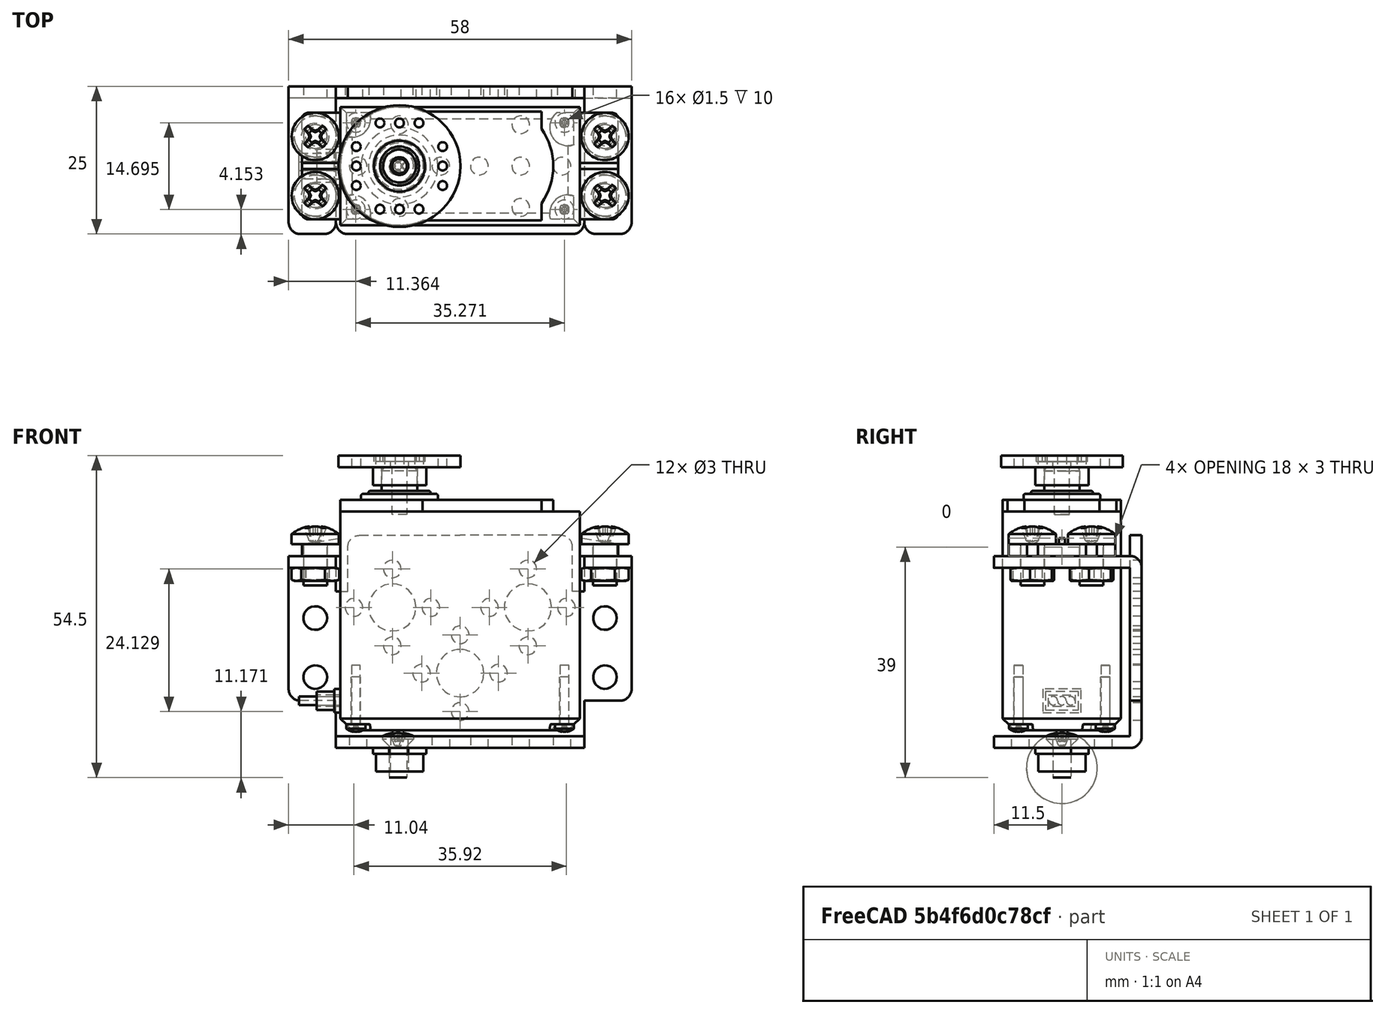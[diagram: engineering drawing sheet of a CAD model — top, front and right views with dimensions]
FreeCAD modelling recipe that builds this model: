
FCSTD DOCUMENT  (FreeCAD 0.19R24276 (Git))
Label: servo_acoplado
License: All rights reserved
LicenseURL: http://en.wikipedia.org/wiki/All_rights_reserved
objects: Part::FeaturePython×13, App::FeaturePython×12, App::DocumentObjectGroup×2
note: 13 computed .brp shape members not serialized (recipe doc carries the construction recipe); baked Part::Feature solids carry a one-line shape summary decoded from their .brp

FEATURE [Part::FeaturePython] b_servo_001_  label="servo_001"  # a2plus imported part (geometry in sourceFile) (typed FeaturePython)
  a2p_Version = V0.1
  fixedPosition = true
  objectType = a2pPart
  sourceFile = .\..\piezas\servo.FCStd
  subassemblyImport = false
  timeLastImport = 1.6204e+09
  updateColors = true
FEATURE [Part::FeaturePython] b_parte_servos_001_  label="parte_servos_001"  # a2plus imported part (geometry in sourceFile) (typed FeaturePython)
  Placement = pos=(2.597e-07,13.5,15) rot=(1,0,0;1.5708rad)
  a2p_Version = V0.1
  fixedPosition = false
  objectType = a2pPart
  sourceFile = .\..\piezas\parte_servos.FCStd
  subassemblyImport = false
  timeLastImport = 1.62041e+09
  updateColors = true
FEATURE [Part::FeaturePython] b_arandela_001_  label="arandela_001"  # a2plus imported part (geometry in sourceFile) (typed FeaturePython)
  Placement = pos=(-10.25,3.87576e-07,-3) rot=(0,1,0;3.14159rad)
  a2p_Version = V0.1
  fixedPosition = false
  objectType = a2pPart
  sourceFile = .\..\piezas\arandela.FCStd
  subassemblyImport = false
  timeLastImport = 1.62024e+09
  updateColors = true
FEATURE [Part::FeaturePython] b_tapa_001_  label="tapa_001"  # a2plus imported part (geometry in sourceFile) (typed FeaturePython)
  Placement = pos=(-10.25,-6.82e-14,46.5) rot=(1,0,0;3.14159rad)
  a2p_Version = V0.1
  fixedPosition = false
  objectType = a2pPart
  sourceFile = .\..\piezas\tapa.FCStd
  subassemblyImport = false
  timeLastImport = 1.62021e+09
  updateColors = true
FEATURE [App::FeaturePython] planeCoincident_001  label="planeCoincident_001__parte_servos_001"  # a2plus constraint (typed FeaturePython)
  Object1 = b_servo_001_
  Object2 = b_parte_servos_001_
  ParentTreeObject = -> b_servo_001_
  SubElement1 = Face61
  SubElement2 = Face84
  Suppressed = false
  Type = plane
  directionConstraint = 1
  offset = 0
FEATURE [App::FeaturePython] planeCoincident_001_mirror  label="planeCoincident_001__servo_001"  # a2plus constraint (typed FeaturePython)
  Object1 = b_servo_001_
  Object2 = b_parte_servos_001_
  ParentTreeObject = -> b_parte_servos_001_
  SubElement1 = Face61
  SubElement2 = Face84
  Suppressed = false
  Type = plane
  directionConstraint = 1
  offset = 0
FEATURE [App::FeaturePython] axisCoincident_001  label="axisCoincident_001__parte_servos_001"  # a2plus constraint (typed FeaturePython)
  Object1 = b_servo_001_
  Object2 = b_parte_servos_001_
  ParentTreeObject = -> b_servo_001_
  SubElement1 = Face84
  SubElement2 = Face82
  Suppressed = false
  Type = axial
  directionConstraint = 0
  lockRotation = false
FEATURE [App::FeaturePython] axisCoincident_001_mirror  label="axisCoincident_001__servo_001"  # a2plus constraint (typed FeaturePython)
  Object1 = b_servo_001_
  Object2 = b_parte_servos_001_
  ParentTreeObject = -> b_parte_servos_001_
  SubElement1 = Face84
  SubElement2 = Face82
  Suppressed = false
  Type = axial
  directionConstraint = 0
  lockRotation = false
FEATURE [App::FeaturePython] planeCoincident_002  label="planeCoincident_002__arandela_001"  # a2plus constraint (typed FeaturePython)
  Object1 = b_parte_servos_001_
  Object2 = b_arandela_001_
  ParentTreeObject = -> b_parte_servos_001_
  SubElement1 = Face4
  SubElement2 = Face2
  Suppressed = false
  Type = plane
  directionConstraint = 1
  offset = 0
FEATURE [App::FeaturePython] planeCoincident_002_mirror  label="planeCoincident_002__parte_servos_001"  # a2plus constraint (typed FeaturePython)
  Object1 = b_parte_servos_001_
  Object2 = b_arandela_001_
  ParentTreeObject = -> b_arandela_001_
  SubElement1 = Face4
  SubElement2 = Face2
  Suppressed = false
  Type = plane
  directionConstraint = 1
  offset = 0
FEATURE [App::FeaturePython] axisCoincident_002  label="axisCoincident_002__parte_servos_001"  # a2plus constraint (typed FeaturePython)
  Object1 = b_arandela_001_
  Object2 = b_parte_servos_001_
  ParentTreeObject = -> b_arandela_001_
  SubElement1 = Face4
  SubElement2 = Face17
  Suppressed = false
  Type = axial
  directionConstraint = 1
  lockRotation = false
FEATURE [App::FeaturePython] axisCoincident_002_mirror  label="axisCoincident_002__arandela_001"  # a2plus constraint (typed FeaturePython)
  Object1 = b_arandela_001_
  Object2 = b_parte_servos_001_
  ParentTreeObject = -> b_parte_servos_001_
  SubElement1 = Face4
  SubElement2 = Face17
  Suppressed = false
  Type = axial
  directionConstraint = 1
  lockRotation = false
FEATURE [App::FeaturePython] axisCoincident_003  label="axisCoincident_003__servo_001"  # a2plus constraint (typed FeaturePython)
  Object1 = b_tapa_001_
  Object2 = b_servo_001_
  ParentTreeObject = -> b_tapa_001_
  SubElement1 = Face21
  SubElement2 = Face141
  Suppressed = false
  Type = axial
  directionConstraint = 1
  lockRotation = false
FEATURE [App::FeaturePython] axisCoincident_003_mirror  label="axisCoincident_003__tapa_001"  # a2plus constraint (typed FeaturePython)
  Object1 = b_tapa_001_
  Object2 = b_servo_001_
  ParentTreeObject = -> b_servo_001_
  SubElement1 = Face21
  SubElement2 = Face141
  Suppressed = false
  Type = axial
  directionConstraint = 1
  lockRotation = false
FEATURE [App::FeaturePython] planeCoincident_003  label="planeCoincident_003__servo_001"  # a2plus constraint (typed FeaturePython)
  Object1 = b_tapa_001_
  Object2 = b_servo_001_
  ParentTreeObject = -> b_tapa_001_
  SubElement1 = Face23
  SubElement2 = Face34
  Suppressed = false
  Type = plane
  directionConstraint = 1
  offset = 0
FEATURE [App::FeaturePython] planeCoincident_003_mirror  label="planeCoincident_003__tapa_001"  # a2plus constraint (typed FeaturePython)
  Object1 = b_tapa_001_
  Object2 = b_servo_001_
  ParentTreeObject = -> b_servo_001_
  SubElement1 = Face23
  SubElement2 = Face34
  Suppressed = false
  Type = plane
  directionConstraint = 1
  offset = 0
FEATURE [Part::FeaturePython] Screw  label="M3x7-Screw"  # Fasteners workbench fastener (typed FeaturePython)
  Placement = pos=(-10.5,3.80571e-07,-1) rot=(0,0,1;0rad)
  baseObject = -> b_parte_servos_001_ [Edge75]
  diameter = 4
  invert = false
  length = 11
  lengthCustom = 7
  matchOuter = true
  offset = 0
  thread = false
  type = 36
FEATURE [Part::FeaturePython] Screw001  label="M4x7-Screw"  # Fasteners workbench fastener (typed FeaturePython)
  Placement = pos=(-24.5,5,31.5) rot=(0,0,1;0rad)
  baseObject = -> b_servo_001_ [Edge725]
  diameter = 6
  invert = true
  length = 12
  lengthCustom = 7
  matchOuter = true
  offset = 0
  thread = false
  type = 34
FEATURE [Part::FeaturePython] Screw002  label="M4x7-Screw001"  # Fasteners workbench fastener (typed FeaturePython)
  Placement = pos=(24.5,5,31.5) rot=(0,0,1;0rad)
  baseObject = -> b_servo_001_ [Edge159]
  diameter = 6
  invert = false
  length = 12
  lengthCustom = 7
  matchOuter = true
  offset = 0
  thread = false
  type = 34
FEATURE [Part::FeaturePython] Screw003  label="M4x7-Screw002"  # Fasteners workbench fastener (typed FeaturePython)
  Placement = pos=(24.5,-5,31.5) rot=(0,0,1;0rad)
  baseObject = -> b_servo_001_ [Edge173]
  diameter = 6
  invert = false
  length = 12
  lengthCustom = 7
  matchOuter = true
  offset = 0
  thread = false
  type = 34
FEATURE [Part::FeaturePython] Screw004  label="M4x7-Screw003"  # Fasteners workbench fastener (typed FeaturePython)
  Placement = pos=(-24.5,-5,31.5) rot=(0,0,1;0rad)
  baseObject = -> b_servo_001_ [Edge233]
  diameter = 6
  invert = true
  length = 12
  lengthCustom = 7
  matchOuter = true
  offset = 0
  thread = false
  type = 34
FEATURE [App::DocumentObjectGroup] Group  label="tornillos"
  Group = -> [Screw,Screw001,Screw002,Screw003,Screw004]
FEATURE [Part::FeaturePython] Nut  label="M4-Nut"  # Fasteners workbench fastener (typed FeaturePython)
  Placement = pos=(-24.5,5,27.5) rot=(-0.456083,0.889937,0;3.14159rad)
  baseObject = -> b_parte_servos_001_ [Edge193]
  diameter = 6
  invert = true
  matchOuter = true
  offset = 0
  thread = false
  type = 9
FEATURE [Part::FeaturePython] Nut001  label="M4-Nut001"  # Fasteners workbench fastener (typed FeaturePython)
  Placement = pos=(-24.5,-5,27.5) rot=(-0.456083,0.889937,0;3.14159rad)
  baseObject = -> b_parte_servos_001_ [Edge192]
  diameter = 6
  invert = true
  matchOuter = true
  offset = 0
  thread = false
  type = 9
FEATURE [Part::FeaturePython] Nut002  label="M4-Nut002"  # Fasteners workbench fastener (typed FeaturePython)
  Placement = pos=(24.5,-5,27.5) rot=(-0.456083,0.889937,0;3.14159rad)
  baseObject = -> b_parte_servos_001_ [Edge219]
  diameter = 6
  invert = true
  matchOuter = true
  offset = 0
  thread = false
  type = 9
FEATURE [Part::FeaturePython] Nut003  label="M4-Nut003"  # Fasteners workbench fastener (typed FeaturePython)
  Placement = pos=(24.5,5,27.5) rot=(-0.456083,0.889937,0;3.14159rad)
  baseObject = -> b_parte_servos_001_ [Edge220]
  diameter = 6
  invert = true
  matchOuter = true
  offset = 0
  thread = false
  type = 9
FEATURE [App::DocumentObjectGroup] Group001  label="tuercas"
  Group = -> [Nut,Nut001,Nut002,Nut003]
